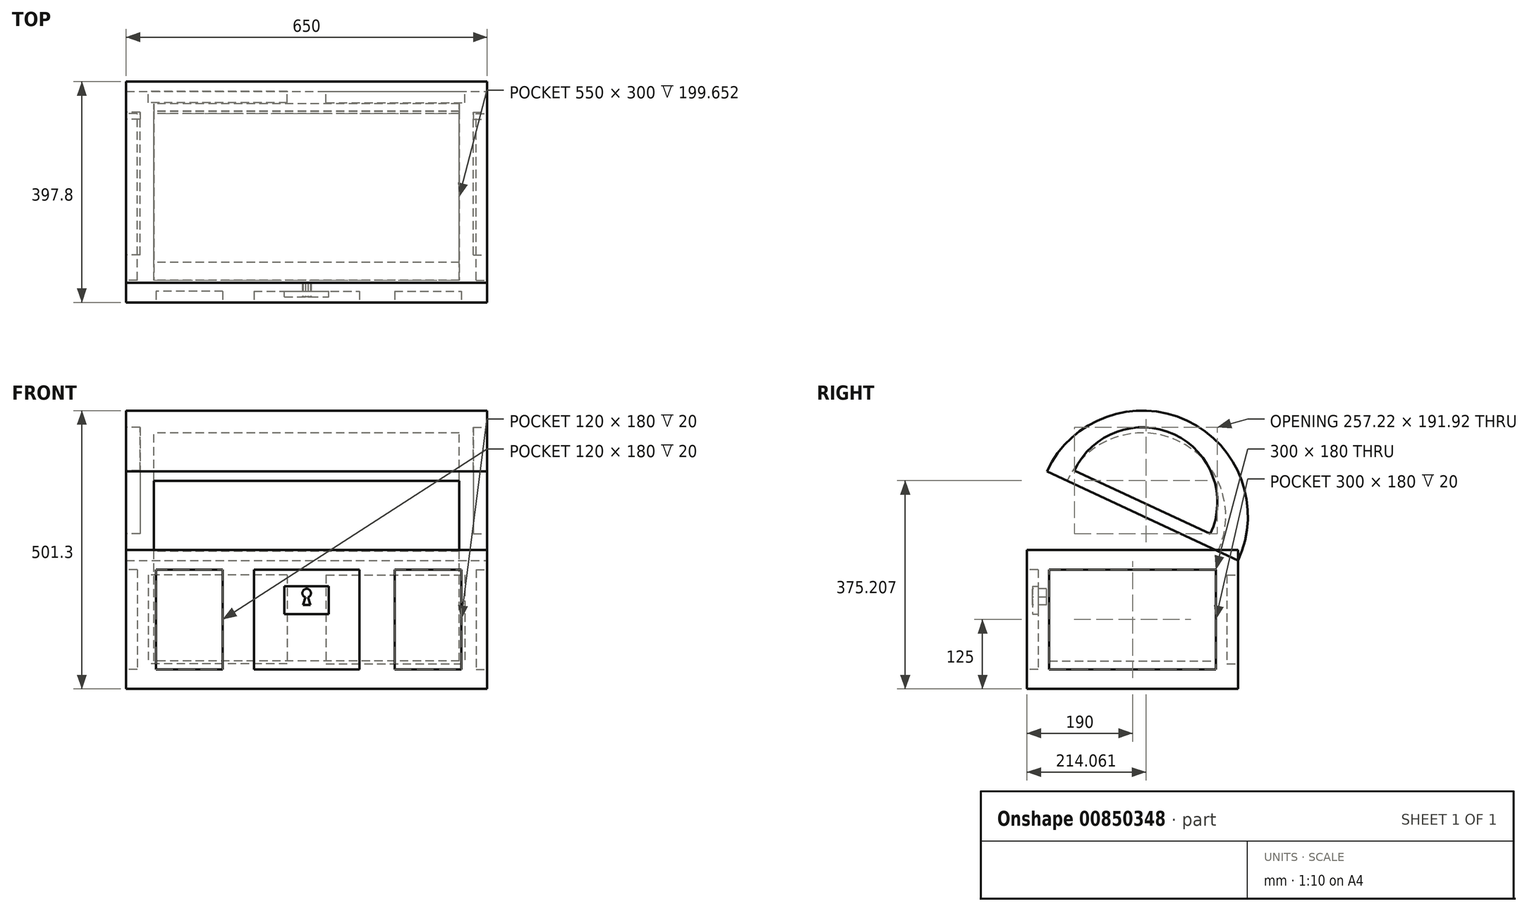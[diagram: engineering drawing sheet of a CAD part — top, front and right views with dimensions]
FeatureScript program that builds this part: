
annotation { "Feature Type Name" : "Feature", "Feature Type Description" : "" }
export const myFeature = defineFeature(function(context is Context, id is Id, definition is map)
    precondition{}
    {
        {
            var Q0;
            Q0=qCreatedBy(makeId("Top.planeOp"),FACE);
            var sketch = newSketch(context, id + "F0", { "sketchPlane" : qUnion([Q0])});
            skLineSegment(sketch, "E0.bottom", {"start": v(-32.5, 19) * mm, "end": v(32.5, 19) * mm});
            skLineSegment(sketch, "E0.top", {"start": v(-32.5, -19) * mm, "end": v(32.5, -19) * mm});
            skLineSegment(sketch, "E0.left", {"start": v(-32.5, 19) * mm, "end": v(-32.5, -19) * mm});
            skLineSegment(sketch, "E0.right", {"start": v(32.5, 19) * mm, "end": v(32.5, -19) * mm});
            skPoint(sketch, "E0.middle", {"position": v(0, 0) * mm});
            skSolve(sketch);
        }
        {
            var Q0;
            Q0=qSketchRegion(id+"F0",true);
            var Q1;
            Q1 = qSketchRegion(id + "F6", true);
            extrude(context, id + "F1", {"entities" : qUnion([Q0, Q1]), "depth" : 25 * mm, "offsetDistance" : 25 * mm});
        }
        {
            var Q0;
            Q0=qCreatedBy(makeId("Right.planeOp"),FACE);
            var sketch = newSketch(context, id + "F2", { "sketchPlane" : qUnion([Q0])});
            skArc(sketch, "E1", {"start": v(-19, 23.1) * mm, "mid": v(-9.8, 48.35) * mm, "end": v(15.44, 39.16) * mm});
            skLineSegment(sketch, "E2", {"start": v(15.44, 39.16) * mm, "end": v(-19, 23.1) * mm});
            skSolve(sketch);
        }
        {
            var Q0;
            Q0=qSketchRegion(id+"F2",true);
            extrude(context, id + "F3", {"entities" : qUnion([Q0]), "endBound" : BoundingType.SYMMETRIC, "depth" : 65 * mm, "offsetDistance" : 25 * mm});
        }
        {
            var Q0;
            Q0=qCreatedBy(makeId("Right.planeOp"),FACE);
            var sketch = newSketch(context, id + "F4", { "sketchPlane" : qUnion([Q0])});
            skArc(sketch, "E3", {"start": v(-15.37, 24.8) * mm, "mid": v(-8.12, 44.72) * mm, "end": v(11.81, 37.47) * mm});
            skLineSegment(sketch, "E4", {"start": v(11.81, 37.47) * mm, "end": v(-15.37, 24.8) * mm});
            skSolve(sketch);
        }
        {
            var Q0;
            Q0=qSketchRegion(id+"F4",true);
            extrude(context, id + "F5", {"entities" : qUnion([Q0]), "operationType" : NewBodyOperationType.REMOVE, "endBound" : BoundingType.SYMMETRIC, "oppositeDirection" : true, "depth" : 55 * mm, "offsetDistance" : 25 * mm});
        }
        {
            var Q0;
            Q0=makeQuery(id+"F3.opExtrude","CAP_FACE",FACE,{"disambiguationData":[OSD([sQuery(id+"F2.wireOp",EDGE,"E1"),sQuery(id+"F2.wireOp",EDGE,"E2")])],"isStart":false});
            var sketch = newSketch(context, id + "F6", { "sketchPlane" : qUnion([Q0])});
            skArc(sketch, "E5", {"start": v(-14.02, 25.42) * mm, "mid": v(-7.49, 43.36) * mm, "end": v(10.46, 36.84) * mm});
            skLineSegment(sketch, "E6", {"start": v(-14.02, 25.42) * mm, "end": v(10.46, 36.84) * mm});
            skSolve(sketch);
        }
        {
            var Q0;
            Q0=qSketchRegion(id+"F6",true);
            extrude(context, id + "F7", {"entities" : qUnion([Q0]), "oppositeDirection" : true, "depth" : 2.5 * mm, "offsetDistance" : 25 * mm});
        }
        {
            var Q0;
            Q0=makeQuery(id+"F7.opExtrude","SWEPT_BODY",BODY,{"disambiguationData":[OSD([sQuery(id+"F6.wireOp",EDGE,"E5"),sQuery(id+"F6.wireOp",EDGE,"E6")])]});
            transform(context, id + "F8", {"entities" : qUnion([Q0]), "transformType" : TransformType.TRANSLATION_3D, "dx" : 0 * mm, "dy" : 0 * mm, "dz" : 2.5 * mm, "makeCopy" : false});
        }
        {
            var Q0;
            Q0=makeQuery(id+"F7.opExtrude","SWEPT_BODY",BODY,{"disambiguationData":[OSD([sQuery(id+"F6.wireOp",EDGE,"E5"),sQuery(id+"F6.wireOp",EDGE,"E6")])]});
            var Q1;
            Q1=qCreatedBy(makeId("Right.planeOp"),FACE);
            mirror(context, id + "F9", {"entities" : qUnion([Q0]), "mirrorPlane" : qUnion([Q1])});
        }
        {
            var Q0;
            Q0=makeQuery(id+"F9.opPattern","COPY",BODY,{"derivedFrom":makeQuery(id+"F7.opExtrude","SWEPT_BODY",BODY,{"disambiguationData":[OSD([sQuery(id+"F6.wireOp",EDGE,"E5"),sQuery(id+"F6.wireOp",EDGE,"E6")])]}),"instanceName":"1"});
            var Q1;
            Q1=makeQuery(id+"F7.opExtrude","SWEPT_BODY",BODY,{"disambiguationData":[OSD([sQuery(id+"F6.wireOp",EDGE,"E5"),sQuery(id+"F6.wireOp",EDGE,"E6")])]});
            var Q2;
            Q2=makeQuery(id+"F3.opExtrude","SWEPT_BODY",BODY,{"disambiguationData":[OSD([sQuery(id+"F2.wireOp",EDGE,"E1"),sQuery(id+"F2.wireOp",EDGE,"E2")])]});
            booleanBodies(context, id + "F10", {"operationType" : BooleanOperationType.SUBTRACTION, "tools" : qUnion([Q0, Q1]), "targets" : qUnion([Q2])});
        }
        {
            var Q0;
            Q0=makeQuery(id+"F1.opExtrude","CAP_FACE",FACE,{"disambiguationData":[OSD([sQuery(id+"F0.wireOp",EDGE,"E0.bottom"),sQuery(id+"F0.wireOp",EDGE,"E0.top"),sQuery(id+"F0.wireOp",EDGE,"E0.left"),sQuery(id+"F0.wireOp",EDGE,"E0.right")])],"isStart":false});
            var sketch = newSketch(context, id + "F11", { "sketchPlane" : qUnion([Q0])});
            skLineSegment(sketch, "E7.bottom", {"start": v(-27.5, 15) * mm, "end": v(27.5, 15) * mm});
            skLineSegment(sketch, "E7.top", {"start": v(-27.5, -15) * mm, "end": v(27.5, -15) * mm});
            skLineSegment(sketch, "E7.left", {"start": v(-27.5, 15) * mm, "end": v(-27.5, -15) * mm});
            skLineSegment(sketch, "E7.right", {"start": v(27.5, 15) * mm, "end": v(27.5, -15) * mm});
            skPoint(sketch, "E7.middle", {"position": v(0, 0) * mm});
            skSolve(sketch);
        }
        {
            var Q0;
            Q0=qSketchRegion(id+"F11",true);
            extrude(context, id + "F12", {"entities" : qUnion([Q0]), "operationType" : NewBodyOperationType.REMOVE, "oppositeDirection" : true, "depth" : 20 * mm, "offsetDistance" : 25 * mm});
        }
        {
            var Q0;
            Q0=makeQuery(id+"F1.opExtrude","SWEPT_FACE",FACE,{"disambiguationData":[OSD([sQuery(id+"F0.wireOp",EDGE,"E0.left")])]});
            var sketch = newSketch(context, id + "F13", { "sketchPlane" : qUnion([Q0])});
            skPoint(sketch, "E8", {"position": v(0, 12.5) * mm});
            skPoint(sketch, "E8.positionSnap0", {"position": v(-19, 12.5) * mm});
            skPoint(sketch, "E8.positionSnap1", {"position": v(0, 25) * mm});
            skLineSegment(sketch, "E9.bottom", {"start": v(-15, 21.5) * mm, "end": v(15, 21.5) * mm});
            skLineSegment(sketch, "E9.top", {"start": v(-15, 3.5) * mm, "end": v(15, 3.5) * mm});
            skLineSegment(sketch, "E9.left", {"start": v(-15, 21.5) * mm, "end": v(-15, 3.5) * mm});
            skLineSegment(sketch, "E9.right", {"start": v(15, 21.5) * mm, "end": v(15, 3.5) * mm});
            skSolve(sketch);
        }
        {
            var Q0;
            Q0=qSketchRegion(id+"F13",true);
            extrude(context, id + "F14", {"entities" : qUnion([Q0]), "oppositeDirection" : true, "depth" : 2 * mm, "offsetDistance" : 25 * mm});
        }
        {
            var Q0;
            Q0=makeQuery(id+"F14.opExtrude","SWEPT_BODY",BODY,{"disambiguationData":[OSD([sQuery(id+"F13.wireOp",EDGE,"E9.bottom"),sQuery(id+"F13.wireOp",EDGE,"E9.top"),sQuery(id+"F13.wireOp",EDGE,"E9.left"),sQuery(id+"F13.wireOp",EDGE,"E9.right")])]});
            var Q1;
            Q1=qCreatedBy(makeId("Right.planeOp"),FACE);
            mirror(context, id + "F15", {"entities" : qUnion([Q0]), "mirrorPlane" : qUnion([Q1])});
        }
        {
            var Q0;
            Q0=makeQuery(id+"F15.opPattern","COPY",BODY,{"derivedFrom":makeQuery(id+"F14.opExtrude","SWEPT_BODY",BODY,{"disambiguationData":[OSD([sQuery(id+"F13.wireOp",EDGE,"E9.bottom"),sQuery(id+"F13.wireOp",EDGE,"E9.top"),sQuery(id+"F13.wireOp",EDGE,"E9.left"),sQuery(id+"F13.wireOp",EDGE,"E9.right")])]}),"instanceName":"1"});
            var Q1;
            Q1=makeQuery(id+"F14.opExtrude","SWEPT_BODY",BODY,{"disambiguationData":[OSD([sQuery(id+"F13.wireOp",EDGE,"E9.bottom"),sQuery(id+"F13.wireOp",EDGE,"E9.top"),sQuery(id+"F13.wireOp",EDGE,"E9.left"),sQuery(id+"F13.wireOp",EDGE,"E9.right")])]});
            var Q2;
            Q2=makeQuery(id+"F1.opExtrude","SWEPT_BODY",BODY,{"disambiguationData":[OSD([sQuery(id+"F0.wireOp",EDGE,"E0.bottom"),sQuery(id+"F0.wireOp",EDGE,"E0.top"),sQuery(id+"F0.wireOp",EDGE,"E0.left"),sQuery(id+"F0.wireOp",EDGE,"E0.right")])]});
            booleanBodies(context, id + "F16", {"operationType" : BooleanOperationType.SUBTRACTION, "tools" : qUnion([Q0, Q1]), "targets" : qUnion([Q2])});
        }
        {
            var Q0;
            Q0=makeQuery(id+"F1.opExtrude","SWEPT_FACE",FACE,{"disambiguationData":[OSD([sQuery(id+"F0.wireOp",EDGE,"E0.bottom")])]});
            var sketch = newSketch(context, id + "F17", { "sketchPlane" : qUnion([Q0])});
            skLineSegment(sketch, "E10.bottom", {"start": v(-9.5, 21.5) * mm, "end": v(9.5, 21.5) * mm});
            skLineSegment(sketch, "E10.top", {"start": v(-9.5, 3.5) * mm, "end": v(9.5, 3.5) * mm});
            skLineSegment(sketch, "E10.left", {"start": v(-9.5, 21.5) * mm, "end": v(-9.5, 3.5) * mm});
            skLineSegment(sketch, "E10.right", {"start": v(9.5, 21.5) * mm, "end": v(9.5, 3.5) * mm});
            skPoint(sketch, "E10.middle", {"position": v(0, 12.5) * mm});
            skPoint(sketch, "E10.middle.positionSnap0", {"position": v(-32.5, 12.5) * mm});
            skPoint(sketch, "E10.middle.positionSnap1", {"position": v(0, 25) * mm});
            skPoint(sketch, "E10.centerSnap0", {"position": v(-32.5, 12.5) * mm});
            skPoint(sketch, "E10.centerSnap1", {"position": v(0, 25) * mm});
            skLineSegment(sketch, "E11.bottom", {"start": v(-15.1, 21.5) * mm, "end": v(-27.1, 21.5) * mm});
            skLineSegment(sketch, "E11.top", {"start": v(-15.1, 3.5) * mm, "end": v(-27.1, 3.5) * mm});
            skLineSegment(sketch, "E11.left", {"start": v(-15.1, 21.5) * mm, "end": v(-15.1, 3.5) * mm});
            skLineSegment(sketch, "E11.right", {"start": v(-27.1, 21.5) * mm, "end": v(-27.1, 3.5) * mm});
            skPoint(sketch, "E11.middle", {"position": v(-21.1, 12.5) * mm});
            skLineSegment(sketch, "E12.bottom", {"start": v(15.85, 21.5) * mm, "end": v(27.85, 21.5) * mm});
            skLineSegment(sketch, "E12.top", {"start": v(15.85, 3.5) * mm, "end": v(27.85, 3.5) * mm});
            skLineSegment(sketch, "E12.left", {"start": v(15.85, 21.5) * mm, "end": v(15.85, 3.5) * mm});
            skLineSegment(sketch, "E12.right", {"start": v(27.85, 21.5) * mm, "end": v(27.85, 3.5) * mm});
            skPoint(sketch, "E12.middle", {"position": v(21.85, 12.5) * mm});
            skPoint(sketch, "E12.middle.positionSnap0", {"position": v(32.5, 12.5) * mm});
            skPoint(sketch, "E12.cornerSnap0", {"position": v(-21.1, 21.5) * mm});
            skPoint(sketch, "E12.centerSnap0", {"position": v(32.5, 12.5) * mm});
            skSolve(sketch);
        }
        {
            var Q0;
            Q0=makeQuery(id+"F17.imprint","IMPRINT",FACE,{"disambiguationData":[TD([[makeQuery(id+"F17.imprint","IMPRINT",EDGE,{"derivedFrom":sQuery(id+"F17.wireOp",EDGE,"E11.bottom")}),1.0]])]});
            var Q1;
            Q1=makeQuery(id+"F17.imprint","IMPRINT",FACE,{"disambiguationData":[TD([[makeQuery(id+"F17.imprint","IMPRINT",EDGE,{"derivedFrom":sQuery(id+"F17.wireOp",EDGE,"E10.bottom")}),-1.0]])]});
            var Q2;
            Q2=makeQuery(id+"F17.imprint","IMPRINT",FACE,{"disambiguationData":[TD([[makeQuery(id+"F17.imprint","IMPRINT",EDGE,{"derivedFrom":sQuery(id+"F17.wireOp",EDGE,"E12.bottom")}),-1.0]])]});
            extrude(context, id + "F18", {"entities" : qUnion([Q0, Q1, Q2]), "operationType" : NewBodyOperationType.REMOVE, "oppositeDirection" : true, "depth" : 2 * mm, "offsetDistance" : 25 * mm});
        }
        {
            var Q0;
            Q0=makeQuery(id+"F1.opExtrude","SWEPT_FACE",FACE,{"disambiguationData":[OSD([sQuery(id+"F0.wireOp",EDGE,"E0.top")])]});
            var sketch = newSketch(context, id + "F19", { "sketchPlane" : qUnion([Q0])});
            skLineSegment(sketch, "E13.bottom", {"start": v(-3.5, 20.5) * mm, "end": v(-28.5, 20.5) * mm});
            skLineSegment(sketch, "E13.top", {"start": v(-3.5, 4.5) * mm, "end": v(-28.5, 4.5) * mm});
            skLineSegment(sketch, "E13.left", {"start": v(-3.5, 20.5) * mm, "end": v(-3.5, 4.5) * mm});
            skLineSegment(sketch, "E13.right", {"start": v(-28.5, 20.5) * mm, "end": v(-28.5, 4.5) * mm});
            skPoint(sketch, "E13.middle", {"position": v(-16, 12.5) * mm});
            skPoint(sketch, "E13.middle.positionSnap0", {"position": v(-32.5, 12.5) * mm});
            skPoint(sketch, "E13.centerSnap0", {"position": v(-32.5, 12.5) * mm});
            skLineSegment(sketch, "E14.bottom", {"start": v(3.5, 20.5) * mm, "end": v(28.5, 20.5) * mm});
            skLineSegment(sketch, "E14.top", {"start": v(3.5, 4.5) * mm, "end": v(28.5, 4.5) * mm});
            skLineSegment(sketch, "E14.left", {"start": v(3.5, 20.5) * mm, "end": v(3.5, 4.5) * mm});
            skLineSegment(sketch, "E14.right", {"start": v(28.5, 20.5) * mm, "end": v(28.5, 4.5) * mm});
            skPoint(sketch, "E14.middle", {"position": v(16, 12.5) * mm});
            skSolve(sketch);
        }
        {
            var Q0;
            Q0=makeQuery(id+"F19.imprint","IMPRINT",FACE,{"disambiguationData":[TD([[makeQuery(id+"F19.imprint","IMPRINT",EDGE,{"derivedFrom":sQuery(id+"F19.wireOp",EDGE,"E13.bottom")}),1.0]])]});
            var Q1;
            Q1=makeQuery(id+"F19.imprint","IMPRINT",FACE,{"disambiguationData":[TD([[makeQuery(id+"F19.imprint","IMPRINT",EDGE,{"derivedFrom":sQuery(id+"F19.wireOp",EDGE,"E14.bottom")}),-1.0]])]});
            extrude(context, id + "F20", {"entities" : qUnion([Q0, Q1]), "operationType" : NewBodyOperationType.REMOVE, "oppositeDirection" : true, "depth" : 2 * mm, "offsetDistance" : 25 * mm});
        }
        {
            var Q0;
            Q0=makeQuery(id+"F18.boolean.opBoolean","COPY",FACE,{"derivedFrom":makeQuery(id+"F18.opExtrude","CAP_FACE",FACE,{"disambiguationData":[OSD([sQuery(id+"F17.wireOp",EDGE,"E10.bottom"),sQuery(id+"F17.wireOp",EDGE,"E10.top"),sQuery(id+"F17.wireOp",EDGE,"E10.left"),sQuery(id+"F17.wireOp",EDGE,"E10.right")])],"isStart":false})});
            var sketch = newSketch(context, id + "F21", { "sketchPlane" : qUnion([Q0])});
            skLineSegment(sketch, "E15.bottom", {"start": v(-4, 18.47) * mm, "end": v(4, 18.47) * mm});
            skLineSegment(sketch, "E15.top", {"start": v(-4, 13.47) * mm, "end": v(4, 13.47) * mm});
            skLineSegment(sketch, "E15.left", {"start": v(-4, 18.47) * mm, "end": v(-4, 13.47) * mm});
            skLineSegment(sketch, "E15.right", {"start": v(4, 18.47) * mm, "end": v(4, 13.47) * mm});
            skPoint(sketch, "E15.middle", {"position": v(0, 15.97) * mm});
            skSolve(sketch);
        }
        {
            var Q0;
            Q0=qSketchRegion(id+"F21",true);
            extrude(context, id + "F22", {"entities" : qUnion([Q0]), "operationType" : NewBodyOperationType.ADD, "depth" : 1 * mm, "offsetDistance" : 25 * mm});
        }
        {
            var Q0;
            Q0=makeQuery(id+"F22.opExtrude","CAP_FACE",FACE,{"disambiguationData":[OSD([sQuery(id+"F21.wireOp",EDGE,"E15.bottom"),sQuery(id+"F21.wireOp",EDGE,"E15.top"),sQuery(id+"F21.wireOp",EDGE,"E15.left"),sQuery(id+"F21.wireOp",EDGE,"E15.right")])],"isStart":false});
            var sketch = newSketch(context, id + "F23", { "sketchPlane" : qUnion([Q0])});
            skCircle(sketch, "E16", {"center": v(0, 17.24) * mm, "radius": 0.78 * mm});
            skLineSegment(sketch, "E17", {"start": v(0, 15.12) * mm, "end": v(-0.65, 15.12) * mm});
            skLineSegment(sketch, "E18", {"start": v(-0.65, 15.12) * mm, "end": v(0, 17.24) * mm});
            skLineSegment(sketch, "E19.MirrorCS", {"start": v(0.65, 15.12) * mm, "end": v(0, 17.24) * mm});
            skLineSegment(sketch, "E20.MirrorCS", {"start": v(0, 15.12) * mm, "end": v(0.65, 15.12) * mm});
            skSolve(sketch);
        }
        {
            var Q0;
            Q0=qSketchRegion(id+"F23",true);
            extrude(context, id + "F24", {"entities" : qUnion([Q0]), "operationType" : NewBodyOperationType.REMOVE, "oppositeDirection" : true, "depth" : 2.5 * mm, "offsetDistance" : 25 * mm});
        }
        {
            var Q0;
            Q0=makeQuery(id+"F1.opExtrude","SWEPT_BODY",BODY,{"disambiguationData":[OSD([sQuery(id+"F0.wireOp",EDGE,"E0.bottom"),sQuery(id+"F0.wireOp",EDGE,"E0.top"),sQuery(id+"F0.wireOp",EDGE,"E0.left"),sQuery(id+"F0.wireOp",EDGE,"E0.right")])]});
            var Q1;
            Q1=makeQuery(id+"F3.opExtrude","SWEPT_BODY",BODY,{"disambiguationData":[OSD([sQuery(id+"F2.wireOp",EDGE,"E1"),sQuery(id+"F2.wireOp",EDGE,"E2")])]});
            var Q2;
            Q2=makeQuery(id+"F1.opExtrude","SWEPT_EDGE",EDGE,{"disambiguationData":[OSD([sQuery(id+"F0.wireOp",EDGE,"E0.top"),sQuery(id+"F0.wireOp",EDGE,"E0.right")])]});
            transform(context, id + "F25", {"entities" : qUnion([Q0, Q1]), "transformType" : TransformType.ROTATION, "transformAxis" : qUnion([Q2]), "angle" : 180 * degree, "makeCopy" : false});
        }
        {
            var Q0;
            Q0=makeQuery(id+"F3.opExtrude","SWEPT_BODY",BODY,{"disambiguationData":[OSD([sQuery(id+"F2.wireOp",EDGE,"E1"),sQuery(id+"F2.wireOp",EDGE,"E2")])]});
            var Q1;
            Q1=makeQuery(id+"F1.opExtrude","SWEPT_BODY",BODY,{"disambiguationData":[OSD([sQuery(id+"F0.wireOp",EDGE,"E0.bottom"),sQuery(id+"F0.wireOp",EDGE,"E0.top"),sQuery(id+"F0.wireOp",EDGE,"E0.left"),sQuery(id+"F0.wireOp",EDGE,"E0.right")])]});
            transform(context, id + "F26", {"entities" : qUnion([Q0, Q1]), "transformType" : TransformType.TRANSLATION_3D, "dx" : -65 * mm, "dy" : 38 * mm, "dz" : 0 * mm, "makeCopy" : false});
        }
        {
            var Q0;
            Q0=makeQuery(id+"F3.opExtrude","SWEPT_BODY",BODY,{"disambiguationData":[OSD([sQuery(id+"F2.wireOp",EDGE,"E1"),sQuery(id+"F2.wireOp",EDGE,"E2")])]});
            var Q1;
            Q1=makeQuery(id+"F1.opExtrude","SWEPT_BODY",BODY,{"disambiguationData":[OSD([sQuery(id+"F0.wireOp",EDGE,"E0.bottom"),sQuery(id+"F0.wireOp",EDGE,"E0.top"),sQuery(id+"F0.wireOp",EDGE,"E0.left"),sQuery(id+"F0.wireOp",EDGE,"E0.right")])]});
            var Q2;
            Q2=qCreatedBy(makeId("Origin.pointOp"),VERTEX);
            transform(context, id + "F27", {"entities" : qUnion([Q0, Q1]), "transformType" : TransformType.SCALE_UNIFORMLY, "scale" : 10, "scalePoint" : qUnion([Q2]), "makeCopy" : false});
        }
    });
